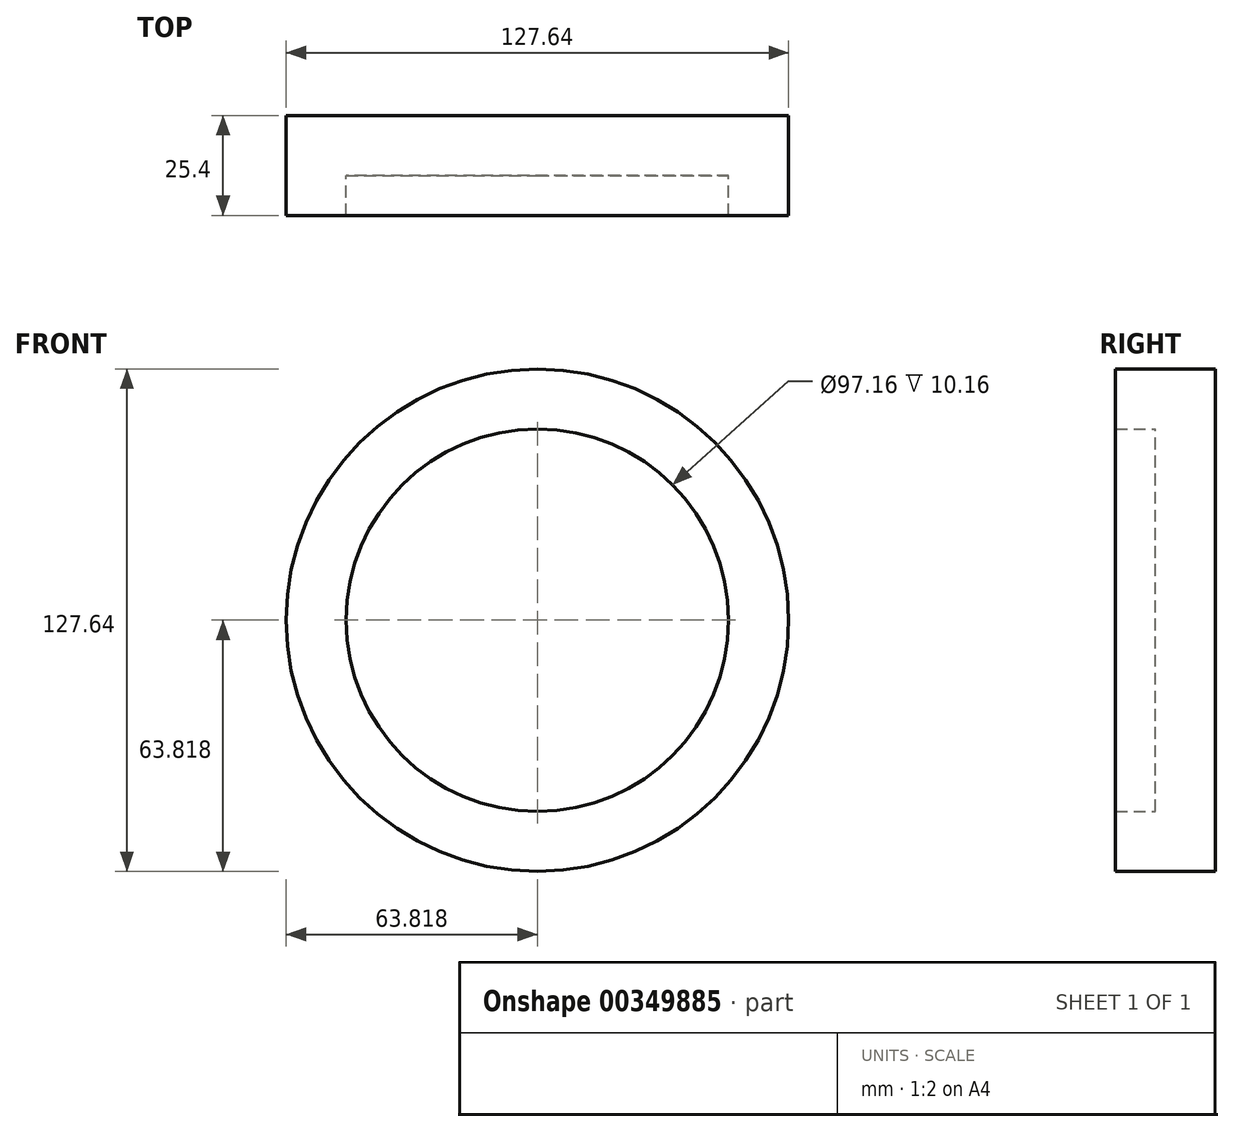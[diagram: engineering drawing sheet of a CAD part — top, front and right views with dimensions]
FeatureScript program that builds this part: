
annotation { "Feature Type Name" : "Feature", "Feature Type Description" : "" }
export const myFeature = defineFeature(function(context is Context, id is Id, definition is map)
    precondition{}
    {
        {
            var Q0;
            Q0=qCreatedBy(makeId("Front.planeOp"),FACE);
            var sketch = newSketch(context, id + "F0", { "sketchPlane" : qUnion([Q0])});
            skCircle(sketch, "E0", {"center": v(-0.14, 0.08) * mm, "radius": 63.82 * mm});
            skSolve(sketch);
        }
        {
            var Q0;
            Q0=makeQuery(id+"F0.imprint","IMPRINT",FACE,{"disambiguationData":[TD([[makeQuery(id+"F0.imprint","IMPRINT",EDGE,{"derivedFrom":sQuery(id+"F0.wireOp",EDGE,"E0")}),1.0]])]});
            var Q1;
            Q1=sQuery(id+"F0.wireOp",EDGE,"E0");
            extrude(context, id + "F1", {"entities" : qUnion([Q0]), "surfaceEntities" : qUnion([Q1]), "depth" : 25.4 * mm});
        }
        {
            var Q0;
            Q0=makeQuery(id+"F1.opExtrude","CAP_FACE",FACE,{"disambiguationData":[OSD([sQuery(id+"F0.wireOp",EDGE,"E0")])],"isStart":false});
            shell(context, id + "F2", {"entities" : qUnion([Q0]), "thickness" : 15.24 * mm});
        }
    });
